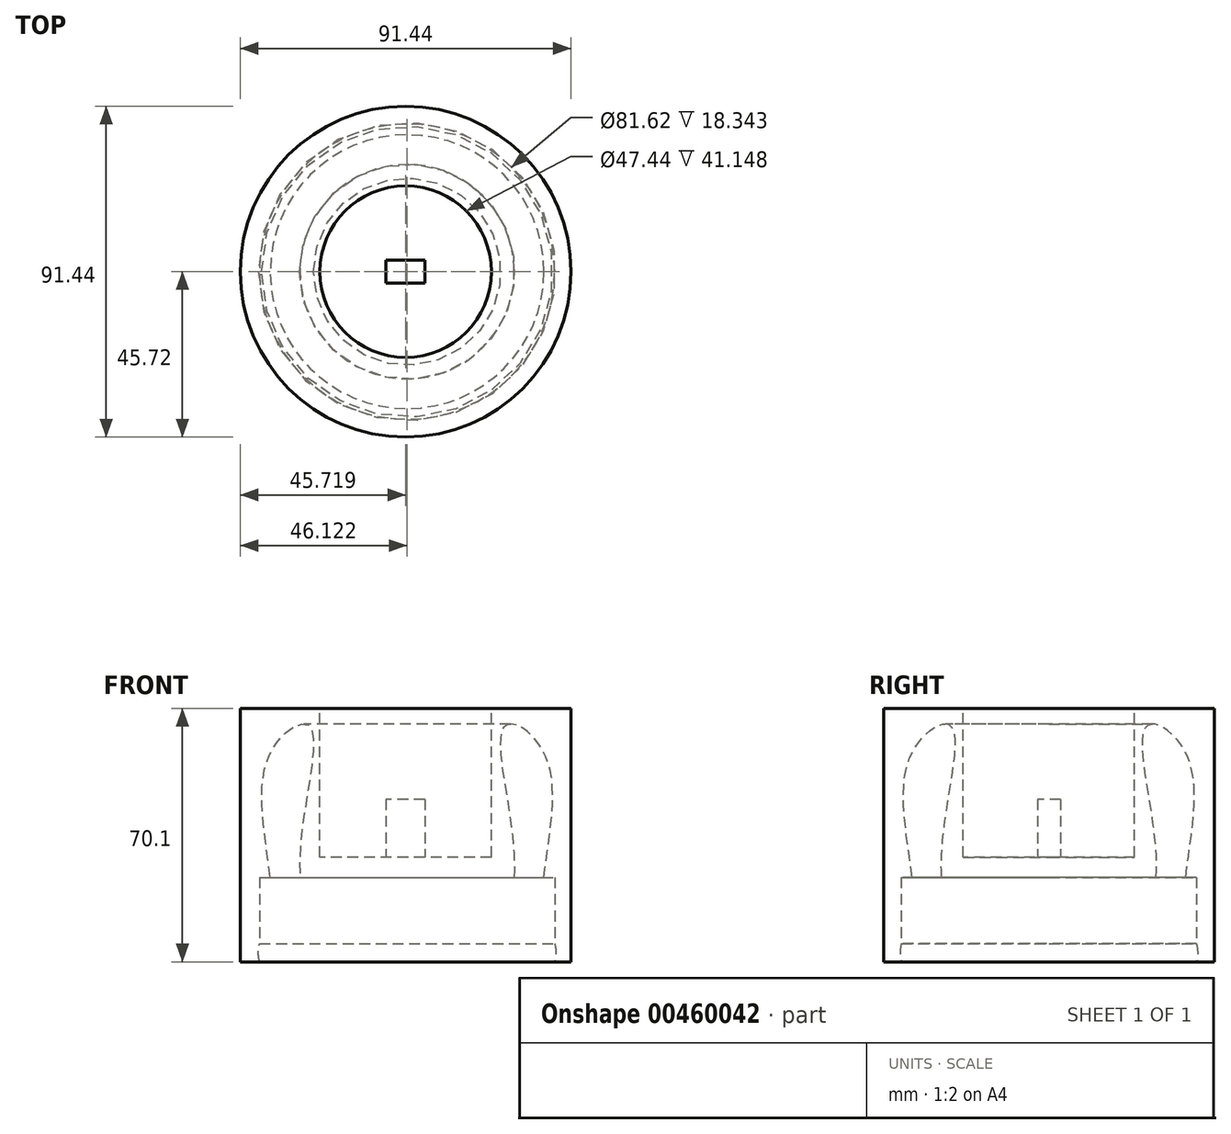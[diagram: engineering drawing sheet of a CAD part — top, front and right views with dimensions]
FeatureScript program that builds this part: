
annotation { "Feature Type Name" : "Feature", "Feature Type Description" : "" }
export const myFeature = defineFeature(function(context is Context, id is Id, definition is map)
    precondition{}
    {
        {
            var Q0;
            Q0=qCreatedBy(makeId("Front.planeOp"),FACE);
            var sketch = newSketch(context, id + "F0", { "sketchPlane" : qUnion([Q0])});
            skFitSpline(sketch, "E0", {"points": [v(-16.63, 0) * mm, v(-13.5, 14.38) * mm, v(-14.88, 54.8) * mm, v(-3.54, 65.63) * mm, v(-3.01, 48.73) * mm, v(-3.8, 16.52) * mm, v(11.15, 0) * mm], "startDerivative": vector(-32.51, 127.64) * mm, "endDerivative": vector(90.2, -149.45) * mm});
            skLineSegment(sketch, "E1", {"start": v(-16.63, 0) * mm, "end": v(11.15, 0) * mm});
            skLineSegment(sketch, "E2", {"start": v(24.18, 0) * mm, "end": v(24.18, 31.22) * mm, "construction": true});
            skSolve(sketch);
        }
        {
            var Q0;
            Q0=makeQuery(id+"F0.imprint","IMPRINT",FACE,{"disambiguationData":[TD([[makeQuery(id+"F0.imprint","IMPRINT",EDGE,{"derivedFrom":sQuery(id+"F0.wireOp",EDGE,"E0")}),-1.0]])]});
            var Q1;
            Q1=sQuery(id+"F0.wireOp",EDGE,"E2");
            revolve(context, id + "F1", {"entities" : qUnion([Q0]), "axis" : qUnion([Q1]), "revolveType" : RevolveType.FULL});
        }
        {
            var Q0;
            Q0=makeQuery(id+"F1.opRevolve","SWEPT_FACE",FACE,{"disambiguationData":[OSD([sQuery(id+"F0.wireOp",EDGE,"E1")])]});
            extrude(context, id + "F2", {"entities" : qUnion([Q0]), "operationType" : NewBodyOperationType.ADD, "oppositeDirection" : true, "depth" : 23.37 * mm, "offsetDistance" : 25.4 * mm});
        }
        {
            var Q0;
            Q0=qCreatedBy(makeId("Top.planeOp"),FACE);
            var sketch = newSketch(context, id + "F3", { "sketchPlane" : qUnion([Q0])});
            skCircle(sketch, "E3", {"center": v(26.25, 0) * mm, "radius": 19.05 * mm});
            skSolve(sketch);
        }
        {
            var Q0;
            Q0 = qSketchRegion(id + "F3", true);
            var Q1;
            Q1=makeQuery(id+"F2.opExtrude","CAP_FACE",FACE,{"disambiguationData":[OSD([sQuery(id+"F0.wireOp",EDGE,"E1")])],"isStart":false});
            extrude(context, id + "F4", {"entities" : qUnion([Q0]), "operationType" : NewBodyOperationType.ADD, "endBound" : BoundingType.UP_TO_SURFACE, "depth" : 25.4 * mm, "endBoundEntityFace" : qUnion([Q1]), "offsetDistance" : 25.4 * mm});
        }
        {
            var Q0;
            Q0=qCreatedBy(makeId("Top.planeOp"),FACE);
            var sketch = newSketch(context, id + "F5", { "sketchPlane" : qUnion([Q0])});
            skCircle(sketch, "E4", {"center": v(23.78, 0) * mm, "radius": 45.72 * mm});
            skSolve(sketch);
        }
        {
            var Q0;
            Q0=makeQuery(id+"F1.opRevolve","SWEPT_BODY",BODY,{"disambiguationData":[OSD([sQuery(id+"F0.wireOp",EDGE,"E0"),sQuery(id+"F0.wireOp",EDGE,"E1")])]});
            transform(context, id + "F6", {"entities" : qUnion([Q0]), "transformType" : TransformType.TRANSLATION_3D, "dx" : 0 * mm, "dy" : 0 * mm, "dz" : 0 * mm, "makeCopy" : true});
        }
        {
            var Q0;
            Q0 = qSketchRegion(id + "F5", true);
            extrude(context, id + "F7", {"entities" : qUnion([Q0]), "depth" : 70.1 * mm, "offsetDistance" : 25.4 * mm});
        }
        {
            var Q0;
            Q0=makeQuery(id+"F1.opRevolve","SWEPT_BODY",BODY,{"disambiguationData":[OSD([sQuery(id+"F0.wireOp",EDGE,"E0"),sQuery(id+"F0.wireOp",EDGE,"E1")])]});
            var Q1;
            Q1=makeQuery(id+"F7.opExtrude","SWEPT_BODY",BODY,{"disambiguationData":[OSD([sQuery(id+"F5.wireOp",EDGE,"E4")])]});
            booleanBodies(context, id + "F8", {"operationType" : BooleanOperationType.SUBTRACTION, "tools" : qUnion([Q0]), "targets" : qUnion([Q1])});
        }
        {
            var Q0;
            Q0=makeQuery(id+"F7.opExtrude","CAP_FACE",FACE,{"disambiguationData":[OSD([sQuery(id+"F5.wireOp",EDGE,"E4")])],"isStart":false});
            var sketch = newSketch(context, id + "F9", { "sketchPlane" : qUnion([Q0])});
            skPoint(sketch, "E5", {"position": v(23.78, 0) * mm});
            skCircle(sketch, "E6", {"center": v(23.78, 0) * mm, "radius": 23.72 * mm});
            skSolve(sketch);
        }
        {
            var Q0;
            Q0 = qSketchRegion(id + "F9", true);
            extrude(context, id + "F10", {"entities" : qUnion([Q0]), "operationType" : NewBodyOperationType.REMOVE, "oppositeDirection" : true, "depth" : 41.15 * mm, "offsetDistance" : 25.4 * mm});
        }
        {
            var Q0;
            Q0=makeQuery(id+"F10.boolean.opBoolean","COPY",FACE,{"derivedFrom":makeQuery(id+"F10.opExtrude","CAP_FACE",FACE,{"disambiguationData":[OSD([sQuery(id+"F9.wireOp",EDGE,"E6")])],"isStart":false})});
            var sketch = newSketch(context, id + "F11", { "sketchPlane" : qUnion([Q0])});
            skLineSegment(sketch, "E7.bottom", {"start": v(29.09, 3.24) * mm, "end": v(18.35, 3.24) * mm});
            skLineSegment(sketch, "E7.top", {"start": v(29.09, -3.11) * mm, "end": v(18.35, -3.11) * mm});
            skLineSegment(sketch, "E7.left", {"start": v(29.09, 3.24) * mm, "end": v(29.09, -3.11) * mm});
            skLineSegment(sketch, "E7.right", {"start": v(18.35, 3.24) * mm, "end": v(18.35, -3.11) * mm});
            skSolve(sketch);
        }
        {
            var Q0;
            Q0 = qSketchRegion(id + "F11", true);
            extrude(context, id + "F12", {"entities" : qUnion([Q0]), "operationType" : NewBodyOperationType.ADD, "depth" : 16 * mm, "offsetDistance" : 25.4 * mm});
        }
    });
